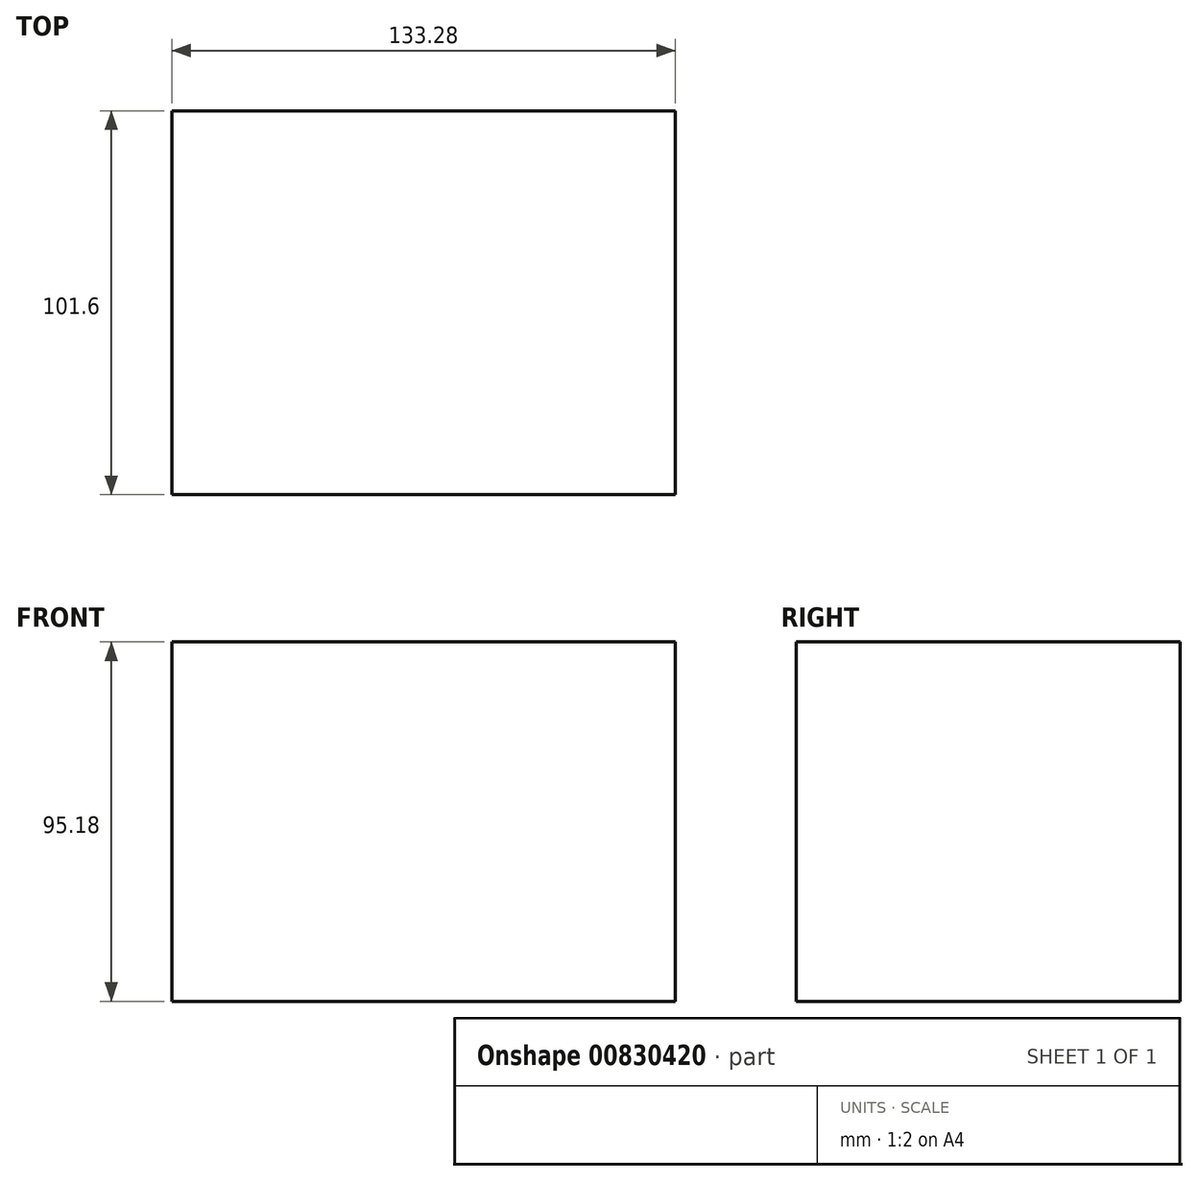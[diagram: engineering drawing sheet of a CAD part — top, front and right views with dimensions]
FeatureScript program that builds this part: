
annotation { "Feature Type Name" : "Feature", "Feature Type Description" : "" }
export const myFeature = defineFeature(function(context is Context, id is Id, definition is map)
    precondition{}
    {
        {
            var Q0;
            Q0=qCreatedBy(makeId("Front.planeOp"),FACE);
            var sketch = newSketch(context, id + "F0", { "sketchPlane" : qUnion([Q0])});
            skLineSegment(sketch, "E0.bottom", {"start": v(-55.6, 62.25) * mm, "end": v(77.68, 62.25) * mm});
            skLineSegment(sketch, "E0.top", {"start": v(-55.6, -32.93) * mm, "end": v(77.68, -32.93) * mm});
            skLineSegment(sketch, "E0.left", {"start": v(-55.6, 62.25) * mm, "end": v(-55.6, -32.93) * mm});
            skLineSegment(sketch, "E0.right", {"start": v(77.68, 62.25) * mm, "end": v(77.68, -32.93) * mm});
            skSolve(sketch);
        }
        {
            var Q0;
            Q0=makeQuery(id+"F0.imprint","IMPRINT",FACE,{"disambiguationData":[TD([[makeQuery(id+"F0.imprint","IMPRINT",EDGE,{"derivedFrom":sQuery(id+"F0.wireOp",EDGE,"E0.bottom")}),-1.0]])]});
            extrude(context, id + "F1", {"entities" : qUnion([Q0]), "depth" : 101.6 * mm, "offsetDistance" : 25.4 * mm});
        }
    });
